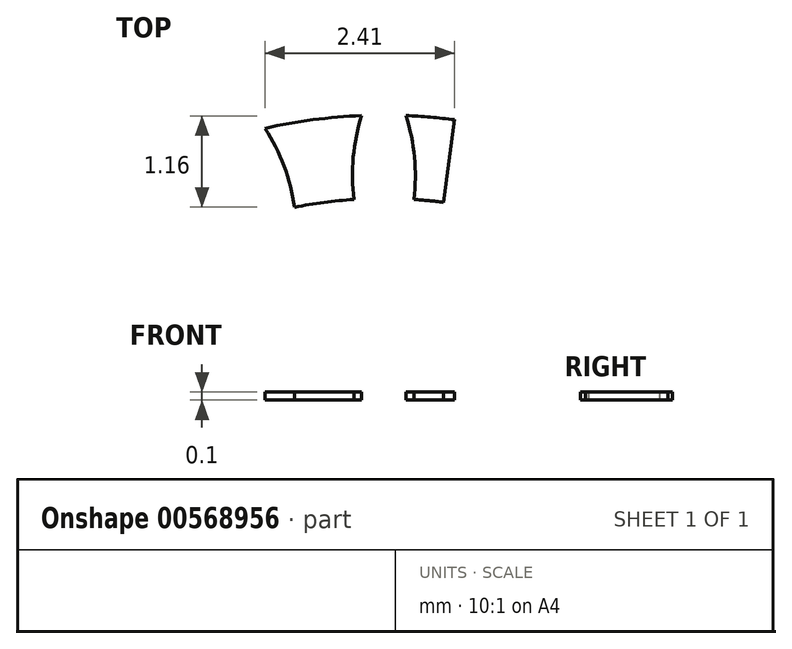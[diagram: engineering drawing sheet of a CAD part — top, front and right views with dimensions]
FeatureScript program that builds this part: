
annotation { "Feature Type Name" : "Feature", "Feature Type Description" : "" }
export const myFeature = defineFeature(function(context is Context, id is Id, definition is map)
    precondition{}
    {
        {
            var Q0;
            Q0=qCreatedBy(makeId("Top.planeOp"),FACE);
            var sketch = newSketch(context, id + "F0", { "sketchPlane" : qUnion([Q0])});
            skCircle(sketch, "E0", {"center": v(0, 0) * mm, "radius": 1.9 * mm});
            skCircle(sketch, "E1.0", {"center": v(0, 0) * mm, "radius": 2.1 * mm});
            skCircle(sketch, "E2", {"center": v(0, 0) * mm, "radius": 6.88 * mm});
            skLineSegment(sketch, "E3", {"start": v(0, 0) * mm, "end": v(0, 6.88) * mm});
            skLineSegment(sketch, "E4", {"start": v(0, 0) * mm, "end": v(0.9, 6.82) * mm});
            skPoint(sketch, "E5", {"position": v(0.38, 5.8) * mm});
            skPoint(sketch, "E6", {"position": v(0.39, 6.34) * mm});
            skPoint(sketch, "E7", {"position": v(0.28, 6.87) * mm});
            skArc(sketch, "E8", {"start": v(0.38, 5.8) * mm, "mid": v(0.57, 5.8) * mm, "end": v(0.76, 5.77) * mm});
            skArc(sketch, "E9", {"start": v(0, 6.88) * mm, "mid": v(0.14, 6.88) * mm, "end": v(0.28, 6.87) * mm});
            skArc(sketch, "E10", {"start": v(0.38, 5.8) * mm, "mid": v(0.39, 6.35) * mm, "end": v(0.28, 6.87) * mm});
            skArc(sketch, "E11.MirrorCS", {"start": v(0, 6.88) * mm, "mid": v(-0.14, 6.88) * mm, "end": v(-0.28, 6.87) * mm});
            skPoint(sketch, "E12.MirrorP", {"position": v(-0.28, 6.87) * mm});
            skPoint(sketch, "E13.MirrorP", {"position": v(-0.38, 5.8) * mm});
            skArc(sketch, "E14.MirrorCS", {"start": v(-0.38, 5.8) * mm, "mid": v(-0.39, 6.35) * mm, "end": v(-0.28, 6.87) * mm});
            skPoint(sketch, "E15.MirrorP", {"position": v(-0.39, 6.34) * mm});
            skArc(sketch, "E16.MirrorCS", {"start": v(-0.38, 5.8) * mm, "mid": v(-0.57, 5.8) * mm, "end": v(-0.76, 5.77) * mm});
            skPoint(sketch, "E17.1.0", {"position": v(-1.87, 5.51) * mm});
            skArc(sketch, "E17.1.1", {"start": v(-1.14, 5.7) * mm, "mid": v(-0.95, 5.74) * mm, "end": v(-0.76, 5.77) * mm});
            skPoint(sketch, "E17.1.2", {"position": v(-1.26, 6.22) * mm});
            skPoint(sketch, "E17.1.3", {"position": v(-2.02, 6.02) * mm});
            skArc(sketch, "E17.1.4", {"start": v(-1.14, 5.7) * mm, "mid": v(-1.27, 6.23) * mm, "end": v(-1.5, 6.71) * mm});
            skPoint(sketch, "E17.1.5", {"position": v(-2.05, 6.57) * mm});
            skPoint(sketch, "E17.1.6", {"position": v(-1.14, 5.7) * mm});
            skArc(sketch, "E17.1.7", {"start": v(-1.87, 5.51) * mm, "mid": v(-2.02, 6.03) * mm, "end": v(-2.05, 6.57) * mm});
            skArc(sketch, "E17.1.8", {"start": v(-1.87, 5.51) * mm, "mid": v(-2.05, 5.45) * mm, "end": v(-2.23, 5.38) * mm});
            skPoint(sketch, "E17.1.9", {"position": v(-1.5, 6.71) * mm});
            skArc(sketch, "E17.1.10", {"start": v(-1.78, 6.64) * mm, "mid": v(-1.64, 6.68) * mm, "end": v(-1.5, 6.71) * mm});
            skArc(sketch, "E17.1.11", {"start": v(-1.78, 6.64) * mm, "mid": v(-1.92, 6.6) * mm, "end": v(-2.05, 6.57) * mm});
            skPoint(sketch, "E17.2.0", {"position": v(-3.23, 4.84) * mm});
            skArc(sketch, "E17.2.1", {"start": v(-2.57, 5.22) * mm, "mid": v(-2.4, 5.3) * mm, "end": v(-2.23, 5.38) * mm});
            skPoint(sketch, "E17.2.2", {"position": v(-2.83, 5.68) * mm});
            skPoint(sketch, "E17.2.3", {"position": v(-3.5, 5.3) * mm});
            skArc(sketch, "E17.2.4", {"start": v(-2.57, 5.22) * mm, "mid": v(-2.84, 5.7) * mm, "end": v(-3.2, 6.1) * mm});
            skPoint(sketch, "E17.2.5", {"position": v(-3.68, 5.81) * mm});
            skPoint(sketch, "E17.2.6", {"position": v(-2.57, 5.22) * mm});
            skArc(sketch, "E17.2.7", {"start": v(-3.23, 4.84) * mm, "mid": v(-3.5, 5.3) * mm, "end": v(-3.68, 5.81) * mm});
            skArc(sketch, "E17.2.8", {"start": v(-3.23, 4.84) * mm, "mid": v(-3.4, 4.73) * mm, "end": v(-3.54, 4.62) * mm});
            skPoint(sketch, "E17.2.9", {"position": v(-3.2, 6.1) * mm});
            skArc(sketch, "E17.2.10", {"start": v(-3.44, 5.96) * mm, "mid": v(-3.32, 6.03) * mm, "end": v(-3.2, 6.1) * mm});
            skArc(sketch, "E17.2.11", {"start": v(-3.44, 5.96) * mm, "mid": v(-3.56, 5.89) * mm, "end": v(-3.68, 5.81) * mm});
            skPoint(sketch, "E17.3.0", {"position": v(-4.38, 3.84) * mm});
            skArc(sketch, "E17.3.1", {"start": v(-3.84, 4.38) * mm, "mid": v(-3.7, 4.5) * mm, "end": v(-3.54, 4.62) * mm});
            skPoint(sketch, "E17.3.2", {"position": v(-4.2, 4.76) * mm});
            skPoint(sketch, "E17.3.3", {"position": v(-4.76, 4.2) * mm});
            skArc(sketch, "E17.3.4", {"start": v(-3.84, 4.38) * mm, "mid": v(-4.21, 4.76) * mm, "end": v(-4.66, 5.06) * mm});
            skPoint(sketch, "E17.3.5", {"position": v(-5.06, 4.66) * mm});
            skPoint(sketch, "E17.3.6", {"position": v(-3.84, 4.38) * mm});
            skArc(sketch, "E17.3.7", {"start": v(-4.38, 3.84) * mm, "mid": v(-4.76, 4.21) * mm, "end": v(-5.06, 4.66) * mm});
            skArc(sketch, "E17.3.8", {"start": v(-4.38, 3.84) * mm, "mid": v(-4.5, 3.7) * mm, "end": v(-4.62, 3.54) * mm});
            skPoint(sketch, "E17.3.9", {"position": v(-4.66, 5.06) * mm});
            skArc(sketch, "E17.3.10", {"start": v(-4.86, 4.86) * mm, "mid": v(-4.76, 4.96) * mm, "end": v(-4.66, 5.06) * mm});
            skArc(sketch, "E17.3.11", {"start": v(-4.86, 4.86) * mm, "mid": v(-4.96, 4.76) * mm, "end": v(-5.06, 4.66) * mm});
            skPoint(sketch, "E17.4.0", {"position": v(-5.22, 2.57) * mm});
            skArc(sketch, "E17.4.1", {"start": v(-4.84, 3.23) * mm, "mid": v(-4.73, 3.4) * mm, "end": v(-4.62, 3.54) * mm});
            skPoint(sketch, "E17.4.2", {"position": v(-5.3, 3.5) * mm});
            skPoint(sketch, "E17.4.3", {"position": v(-5.68, 2.83) * mm});
            skArc(sketch, "E17.4.4", {"start": v(-4.84, 3.23) * mm, "mid": v(-5.3, 3.5) * mm, "end": v(-5.81, 3.68) * mm});
            skPoint(sketch, "E17.4.5", {"position": v(-6.1, 3.2) * mm});
            skPoint(sketch, "E17.4.6", {"position": v(-4.84, 3.23) * mm});
            skArc(sketch, "E17.4.7", {"start": v(-5.22, 2.57) * mm, "mid": v(-5.7, 2.84) * mm, "end": v(-6.1, 3.2) * mm});
            skArc(sketch, "E17.4.8", {"start": v(-5.22, 2.57) * mm, "mid": v(-5.3, 2.4) * mm, "end": v(-5.38, 2.23) * mm});
            skPoint(sketch, "E17.4.9", {"position": v(-5.81, 3.68) * mm});
            skArc(sketch, "E17.4.10", {"start": v(-5.96, 3.44) * mm, "mid": v(-5.89, 3.56) * mm, "end": v(-5.81, 3.68) * mm});
            skArc(sketch, "E17.4.11", {"start": v(-5.96, 3.44) * mm, "mid": v(-6.03, 3.32) * mm, "end": v(-6.1, 3.2) * mm});
            skPoint(sketch, "E17.5.0", {"position": v(-5.7, 1.14) * mm});
            skArc(sketch, "E17.5.1", {"start": v(-5.51, 1.87) * mm, "mid": v(-5.45, 2.05) * mm, "end": v(-5.38, 2.23) * mm});
            skPoint(sketch, "E17.5.2", {"position": v(-6.02, 2.02) * mm});
            skPoint(sketch, "E17.5.3", {"position": v(-6.22, 1.26) * mm});
            skArc(sketch, "E17.5.4", {"start": v(-5.51, 1.87) * mm, "mid": v(-6.03, 2.02) * mm, "end": v(-6.57, 2.05) * mm});
            skPoint(sketch, "E17.5.5", {"position": v(-6.71, 1.5) * mm});
            skPoint(sketch, "E17.5.6", {"position": v(-5.51, 1.87) * mm});
            skArc(sketch, "E17.5.7", {"start": v(-5.7, 1.14) * mm, "mid": v(-6.23, 1.27) * mm, "end": v(-6.71, 1.5) * mm});
            skArc(sketch, "E17.5.8", {"start": v(-5.7, 1.14) * mm, "mid": v(-5.74, 0.95) * mm, "end": v(-5.77, 0.76) * mm});
            skPoint(sketch, "E17.5.9", {"position": v(-6.57, 2.05) * mm});
            skArc(sketch, "E17.5.10", {"start": v(-6.64, 1.78) * mm, "mid": v(-6.6, 1.92) * mm, "end": v(-6.57, 2.05) * mm});
            skArc(sketch, "E17.5.11", {"start": v(-6.64, 1.78) * mm, "mid": v(-6.68, 1.64) * mm, "end": v(-6.71, 1.5) * mm});
            skPoint(sketch, "E17.6.0", {"position": v(-5.8, -0.38) * mm});
            skArc(sketch, "E17.6.1", {"start": v(-5.8, 0.38) * mm, "mid": v(-5.8, 0.57) * mm, "end": v(-5.77, 0.76) * mm});
            skPoint(sketch, "E17.6.2", {"position": v(-6.34, 0.39) * mm});
            skPoint(sketch, "E17.6.3", {"position": v(-6.34, -0.39) * mm});
            skArc(sketch, "E17.6.4", {"start": v(-5.8, 0.38) * mm, "mid": v(-6.35, 0.39) * mm, "end": v(-6.87, 0.28) * mm});
            skPoint(sketch, "E17.6.5", {"position": v(-6.87, -0.28) * mm});
            skPoint(sketch, "E17.6.6", {"position": v(-5.8, 0.38) * mm});
            skArc(sketch, "E17.6.7", {"start": v(-5.8, -0.38) * mm, "mid": v(-6.35, -0.39) * mm, "end": v(-6.87, -0.28) * mm});
            skArc(sketch, "E17.6.8", {"start": v(-5.8, -0.38) * mm, "mid": v(-5.8, -0.57) * mm, "end": v(-5.77, -0.76) * mm});
            skPoint(sketch, "E17.6.9", {"position": v(-6.87, 0.28) * mm});
            skArc(sketch, "E17.6.10", {"start": v(-6.88, 0) * mm, "mid": v(-6.88, 0.14) * mm, "end": v(-6.87, 0.28) * mm});
            skArc(sketch, "E17.6.11", {"start": v(-6.88, 0) * mm, "mid": v(-6.88, -0.14) * mm, "end": v(-6.87, -0.28) * mm});
            skPoint(sketch, "E17.7.0", {"position": v(-5.51, -1.87) * mm});
            skArc(sketch, "E17.7.1", {"start": v(-5.7, -1.14) * mm, "mid": v(-5.74, -0.95) * mm, "end": v(-5.77, -0.76) * mm});
            skPoint(sketch, "E17.7.2", {"position": v(-6.22, -1.26) * mm});
            skPoint(sketch, "E17.7.3", {"position": v(-6.02, -2.02) * mm});
            skArc(sketch, "E17.7.4", {"start": v(-5.7, -1.14) * mm, "mid": v(-6.23, -1.27) * mm, "end": v(-6.71, -1.5) * mm});
            skPoint(sketch, "E17.7.5", {"position": v(-6.57, -2.05) * mm});
            skPoint(sketch, "E17.7.6", {"position": v(-5.7, -1.14) * mm});
            skArc(sketch, "E17.7.7", {"start": v(-5.51, -1.87) * mm, "mid": v(-6.03, -2.02) * mm, "end": v(-6.57, -2.05) * mm});
            skArc(sketch, "E17.7.8", {"start": v(-5.51, -1.87) * mm, "mid": v(-5.45, -2.05) * mm, "end": v(-5.38, -2.23) * mm});
            skPoint(sketch, "E17.7.9", {"position": v(-6.71, -1.5) * mm});
            skArc(sketch, "E17.7.10", {"start": v(-6.64, -1.78) * mm, "mid": v(-6.68, -1.64) * mm, "end": v(-6.71, -1.5) * mm});
            skArc(sketch, "E17.7.11", {"start": v(-6.64, -1.78) * mm, "mid": v(-6.6, -1.92) * mm, "end": v(-6.57, -2.05) * mm});
            skPoint(sketch, "E17.8.0", {"position": v(-4.84, -3.23) * mm});
            skArc(sketch, "E17.8.1", {"start": v(-5.22, -2.57) * mm, "mid": v(-5.3, -2.4) * mm, "end": v(-5.38, -2.23) * mm});
            skPoint(sketch, "E17.8.2", {"position": v(-5.68, -2.83) * mm});
            skPoint(sketch, "E17.8.3", {"position": v(-5.3, -3.5) * mm});
            skArc(sketch, "E17.8.4", {"start": v(-5.22, -2.57) * mm, "mid": v(-5.7, -2.84) * mm, "end": v(-6.1, -3.2) * mm});
            skPoint(sketch, "E17.8.5", {"position": v(-5.81, -3.68) * mm});
            skPoint(sketch, "E17.8.6", {"position": v(-5.22, -2.57) * mm});
            skArc(sketch, "E17.8.7", {"start": v(-4.84, -3.23) * mm, "mid": v(-5.3, -3.5) * mm, "end": v(-5.81, -3.68) * mm});
            skArc(sketch, "E17.8.8", {"start": v(-4.84, -3.23) * mm, "mid": v(-4.73, -3.4) * mm, "end": v(-4.62, -3.54) * mm});
            skPoint(sketch, "E17.8.9", {"position": v(-6.1, -3.2) * mm});
            skArc(sketch, "E17.8.10", {"start": v(-5.96, -3.44) * mm, "mid": v(-6.03, -3.32) * mm, "end": v(-6.1, -3.2) * mm});
            skArc(sketch, "E17.8.11", {"start": v(-5.96, -3.44) * mm, "mid": v(-5.89, -3.56) * mm, "end": v(-5.81, -3.68) * mm});
            skPoint(sketch, "E17.9.0", {"position": v(-3.84, -4.38) * mm});
            skArc(sketch, "E17.9.1", {"start": v(-4.38, -3.84) * mm, "mid": v(-4.5, -3.7) * mm, "end": v(-4.62, -3.54) * mm});
            skPoint(sketch, "E17.9.2", {"position": v(-4.76, -4.2) * mm});
            skPoint(sketch, "E17.9.3", {"position": v(-4.2, -4.76) * mm});
            skArc(sketch, "E17.9.4", {"start": v(-4.38, -3.84) * mm, "mid": v(-4.76, -4.21) * mm, "end": v(-5.06, -4.66) * mm});
            skPoint(sketch, "E17.9.5", {"position": v(-4.66, -5.06) * mm});
            skPoint(sketch, "E17.9.6", {"position": v(-4.38, -3.84) * mm});
            skArc(sketch, "E17.9.7", {"start": v(-3.84, -4.38) * mm, "mid": v(-4.21, -4.76) * mm, "end": v(-4.66, -5.06) * mm});
            skArc(sketch, "E17.9.8", {"start": v(-3.84, -4.38) * mm, "mid": v(-3.7, -4.5) * mm, "end": v(-3.54, -4.62) * mm});
            skPoint(sketch, "E17.9.9", {"position": v(-5.06, -4.66) * mm});
            skArc(sketch, "E17.9.10", {"start": v(-4.86, -4.86) * mm, "mid": v(-4.96, -4.76) * mm, "end": v(-5.06, -4.66) * mm});
            skArc(sketch, "E17.9.11", {"start": v(-4.86, -4.86) * mm, "mid": v(-4.76, -4.96) * mm, "end": v(-4.66, -5.06) * mm});
            skPoint(sketch, "E17.10.0", {"position": v(-2.57, -5.22) * mm});
            skArc(sketch, "E17.10.1", {"start": v(-3.23, -4.84) * mm, "mid": v(-3.4, -4.73) * mm, "end": v(-3.54, -4.62) * mm});
            skPoint(sketch, "E17.10.2", {"position": v(-3.5, -5.3) * mm});
            skPoint(sketch, "E17.10.3", {"position": v(-2.83, -5.68) * mm});
            skArc(sketch, "E17.10.4", {"start": v(-3.23, -4.84) * mm, "mid": v(-3.5, -5.3) * mm, "end": v(-3.68, -5.81) * mm});
            skPoint(sketch, "E17.10.5", {"position": v(-3.2, -6.1) * mm});
            skPoint(sketch, "E17.10.6", {"position": v(-3.23, -4.84) * mm});
            skArc(sketch, "E17.10.7", {"start": v(-2.57, -5.22) * mm, "mid": v(-2.84, -5.7) * mm, "end": v(-3.2, -6.1) * mm});
            skArc(sketch, "E17.10.8", {"start": v(-2.57, -5.22) * mm, "mid": v(-2.4, -5.3) * mm, "end": v(-2.23, -5.38) * mm});
            skPoint(sketch, "E17.10.9", {"position": v(-3.68, -5.81) * mm});
            skArc(sketch, "E17.10.10", {"start": v(-3.44, -5.96) * mm, "mid": v(-3.56, -5.89) * mm, "end": v(-3.68, -5.81) * mm});
            skArc(sketch, "E17.10.11", {"start": v(-3.44, -5.96) * mm, "mid": v(-3.32, -6.03) * mm, "end": v(-3.2, -6.1) * mm});
            skPoint(sketch, "E17.11.0", {"position": v(-1.14, -5.7) * mm});
            skArc(sketch, "E17.11.1", {"start": v(-1.87, -5.51) * mm, "mid": v(-2.05, -5.45) * mm, "end": v(-2.23, -5.38) * mm});
            skPoint(sketch, "E17.11.2", {"position": v(-2.02, -6.02) * mm});
            skPoint(sketch, "E17.11.3", {"position": v(-1.26, -6.22) * mm});
            skArc(sketch, "E17.11.4", {"start": v(-1.87, -5.51) * mm, "mid": v(-2.02, -6.03) * mm, "end": v(-2.05, -6.57) * mm});
            skPoint(sketch, "E17.11.5", {"position": v(-1.5, -6.71) * mm});
            skPoint(sketch, "E17.11.6", {"position": v(-1.87, -5.51) * mm});
            skArc(sketch, "E17.11.7", {"start": v(-1.14, -5.7) * mm, "mid": v(-1.27, -6.23) * mm, "end": v(-1.5, -6.71) * mm});
            skArc(sketch, "E17.11.8", {"start": v(-1.14, -5.7) * mm, "mid": v(-0.95, -5.74) * mm, "end": v(-0.76, -5.77) * mm});
            skPoint(sketch, "E17.11.9", {"position": v(-2.05, -6.57) * mm});
            skArc(sketch, "E17.11.10", {"start": v(-1.78, -6.64) * mm, "mid": v(-1.92, -6.6) * mm, "end": v(-2.05, -6.57) * mm});
            skArc(sketch, "E17.11.11", {"start": v(-1.78, -6.64) * mm, "mid": v(-1.64, -6.68) * mm, "end": v(-1.5, -6.71) * mm});
            skPoint(sketch, "E17.12.0", {"position": v(0.38, -5.8) * mm});
            skArc(sketch, "E17.12.1", {"start": v(-0.38, -5.8) * mm, "mid": v(-0.57, -5.8) * mm, "end": v(-0.76, -5.77) * mm});
            skPoint(sketch, "E17.12.2", {"position": v(-0.39, -6.34) * mm});
            skPoint(sketch, "E17.12.3", {"position": v(0.39, -6.34) * mm});
            skArc(sketch, "E17.12.4", {"start": v(-0.38, -5.8) * mm, "mid": v(-0.39, -6.35) * mm, "end": v(-0.28, -6.87) * mm});
            skPoint(sketch, "E17.12.5", {"position": v(0.28, -6.87) * mm});
            skPoint(sketch, "E17.12.6", {"position": v(-0.38, -5.8) * mm});
            skArc(sketch, "E17.12.7", {"start": v(0.38, -5.8) * mm, "mid": v(0.39, -6.35) * mm, "end": v(0.28, -6.87) * mm});
            skArc(sketch, "E17.12.8", {"start": v(0.38, -5.8) * mm, "mid": v(0.57, -5.8) * mm, "end": v(0.76, -5.77) * mm});
            skPoint(sketch, "E17.12.9", {"position": v(-0.28, -6.87) * mm});
            skArc(sketch, "E17.12.10", {"start": v(0, -6.88) * mm, "mid": v(-0.14, -6.88) * mm, "end": v(-0.28, -6.87) * mm});
            skArc(sketch, "E17.12.11", {"start": v(0, -6.88) * mm, "mid": v(0.14, -6.88) * mm, "end": v(0.28, -6.87) * mm});
            skPoint(sketch, "E17.13.0", {"position": v(1.87, -5.51) * mm});
            skArc(sketch, "E17.13.1", {"start": v(1.14, -5.7) * mm, "mid": v(0.95, -5.74) * mm, "end": v(0.76, -5.77) * mm});
            skPoint(sketch, "E17.13.2", {"position": v(1.26, -6.22) * mm});
            skPoint(sketch, "E17.13.3", {"position": v(2.02, -6.02) * mm});
            skArc(sketch, "E17.13.4", {"start": v(1.14, -5.7) * mm, "mid": v(1.27, -6.23) * mm, "end": v(1.5, -6.71) * mm});
            skPoint(sketch, "E17.13.5", {"position": v(2.05, -6.57) * mm});
            skPoint(sketch, "E17.13.6", {"position": v(1.14, -5.7) * mm});
            skArc(sketch, "E17.13.7", {"start": v(1.87, -5.51) * mm, "mid": v(2.02, -6.03) * mm, "end": v(2.05, -6.57) * mm});
            skArc(sketch, "E17.13.8", {"start": v(1.87, -5.51) * mm, "mid": v(2.05, -5.45) * mm, "end": v(2.23, -5.38) * mm});
            skPoint(sketch, "E17.13.9", {"position": v(1.5, -6.71) * mm});
            skArc(sketch, "E17.13.10", {"start": v(1.78, -6.64) * mm, "mid": v(1.64, -6.68) * mm, "end": v(1.5, -6.71) * mm});
            skArc(sketch, "E17.13.11", {"start": v(1.78, -6.64) * mm, "mid": v(1.92, -6.6) * mm, "end": v(2.05, -6.57) * mm});
            skPoint(sketch, "E17.14.0", {"position": v(3.23, -4.84) * mm});
            skArc(sketch, "E17.14.1", {"start": v(2.57, -5.22) * mm, "mid": v(2.4, -5.3) * mm, "end": v(2.23, -5.38) * mm});
            skPoint(sketch, "E17.14.2", {"position": v(2.83, -5.68) * mm});
            skPoint(sketch, "E17.14.3", {"position": v(3.5, -5.3) * mm});
            skArc(sketch, "E17.14.4", {"start": v(2.57, -5.22) * mm, "mid": v(2.84, -5.7) * mm, "end": v(3.2, -6.1) * mm});
            skPoint(sketch, "E17.14.5", {"position": v(3.68, -5.81) * mm});
            skPoint(sketch, "E17.14.6", {"position": v(2.57, -5.22) * mm});
            skArc(sketch, "E17.14.7", {"start": v(3.23, -4.84) * mm, "mid": v(3.5, -5.3) * mm, "end": v(3.68, -5.81) * mm});
            skArc(sketch, "E17.14.8", {"start": v(3.23, -4.84) * mm, "mid": v(3.4, -4.73) * mm, "end": v(3.54, -4.62) * mm});
            skPoint(sketch, "E17.14.9", {"position": v(3.2, -6.1) * mm});
            skArc(sketch, "E17.14.10", {"start": v(3.44, -5.96) * mm, "mid": v(3.32, -6.03) * mm, "end": v(3.2, -6.1) * mm});
            skArc(sketch, "E17.14.11", {"start": v(3.44, -5.96) * mm, "mid": v(3.56, -5.89) * mm, "end": v(3.68, -5.81) * mm});
            skPoint(sketch, "E17.15.0", {"position": v(4.38, -3.84) * mm});
            skArc(sketch, "E17.15.1", {"start": v(3.84, -4.38) * mm, "mid": v(3.7, -4.5) * mm, "end": v(3.54, -4.62) * mm});
            skPoint(sketch, "E17.15.2", {"position": v(4.2, -4.76) * mm});
            skPoint(sketch, "E17.15.3", {"position": v(4.76, -4.2) * mm});
            skArc(sketch, "E17.15.4", {"start": v(3.84, -4.38) * mm, "mid": v(4.21, -4.76) * mm, "end": v(4.66, -5.06) * mm});
            skPoint(sketch, "E17.15.5", {"position": v(5.06, -4.66) * mm});
            skPoint(sketch, "E17.15.6", {"position": v(3.84, -4.38) * mm});
            skArc(sketch, "E17.15.7", {"start": v(4.38, -3.84) * mm, "mid": v(4.76, -4.21) * mm, "end": v(5.06, -4.66) * mm});
            skArc(sketch, "E17.15.8", {"start": v(4.38, -3.84) * mm, "mid": v(4.5, -3.7) * mm, "end": v(4.62, -3.54) * mm});
            skPoint(sketch, "E17.15.9", {"position": v(4.66, -5.06) * mm});
            skArc(sketch, "E17.15.10", {"start": v(4.86, -4.86) * mm, "mid": v(4.76, -4.96) * mm, "end": v(4.66, -5.06) * mm});
            skArc(sketch, "E17.15.11", {"start": v(4.86, -4.86) * mm, "mid": v(4.96, -4.76) * mm, "end": v(5.06, -4.66) * mm});
            skPoint(sketch, "E17.16.0", {"position": v(5.22, -2.57) * mm});
            skArc(sketch, "E17.16.1", {"start": v(4.84, -3.23) * mm, "mid": v(4.73, -3.4) * mm, "end": v(4.62, -3.54) * mm});
            skPoint(sketch, "E17.16.2", {"position": v(5.3, -3.5) * mm});
            skPoint(sketch, "E17.16.3", {"position": v(5.68, -2.83) * mm});
            skArc(sketch, "E17.16.4", {"start": v(4.84, -3.23) * mm, "mid": v(5.3, -3.5) * mm, "end": v(5.81, -3.68) * mm});
            skPoint(sketch, "E17.16.5", {"position": v(6.1, -3.2) * mm});
            skPoint(sketch, "E17.16.6", {"position": v(4.84, -3.23) * mm});
            skArc(sketch, "E17.16.7", {"start": v(5.22, -2.57) * mm, "mid": v(5.7, -2.84) * mm, "end": v(6.1, -3.2) * mm});
            skArc(sketch, "E17.16.8", {"start": v(5.22, -2.57) * mm, "mid": v(5.3, -2.4) * mm, "end": v(5.38, -2.23) * mm});
            skPoint(sketch, "E17.16.9", {"position": v(5.81, -3.68) * mm});
            skArc(sketch, "E17.16.10", {"start": v(5.96, -3.44) * mm, "mid": v(5.89, -3.56) * mm, "end": v(5.81, -3.68) * mm});
            skArc(sketch, "E17.16.11", {"start": v(5.96, -3.44) * mm, "mid": v(6.03, -3.32) * mm, "end": v(6.1, -3.2) * mm});
            skPoint(sketch, "E17.17.0", {"position": v(5.7, -1.14) * mm});
            skArc(sketch, "E17.17.1", {"start": v(5.51, -1.87) * mm, "mid": v(5.45, -2.05) * mm, "end": v(5.38, -2.23) * mm});
            skPoint(sketch, "E17.17.2", {"position": v(6.02, -2.02) * mm});
            skPoint(sketch, "E17.17.3", {"position": v(6.22, -1.26) * mm});
            skArc(sketch, "E17.17.4", {"start": v(5.51, -1.87) * mm, "mid": v(6.03, -2.02) * mm, "end": v(6.57, -2.05) * mm});
            skPoint(sketch, "E17.17.5", {"position": v(6.71, -1.5) * mm});
            skPoint(sketch, "E17.17.6", {"position": v(5.51, -1.87) * mm});
            skArc(sketch, "E17.17.7", {"start": v(5.7, -1.14) * mm, "mid": v(6.23, -1.27) * mm, "end": v(6.71, -1.5) * mm});
            skArc(sketch, "E17.17.8", {"start": v(5.7, -1.14) * mm, "mid": v(5.74, -0.95) * mm, "end": v(5.77, -0.76) * mm});
            skPoint(sketch, "E17.17.9", {"position": v(6.57, -2.05) * mm});
            skArc(sketch, "E17.17.10", {"start": v(6.64, -1.78) * mm, "mid": v(6.6, -1.92) * mm, "end": v(6.57, -2.05) * mm});
            skArc(sketch, "E17.17.11", {"start": v(6.64, -1.78) * mm, "mid": v(6.68, -1.64) * mm, "end": v(6.71, -1.5) * mm});
            skPoint(sketch, "E17.18.0", {"position": v(5.8, 0.38) * mm});
            skArc(sketch, "E17.18.1", {"start": v(5.8, -0.38) * mm, "mid": v(5.8, -0.57) * mm, "end": v(5.77, -0.76) * mm});
            skPoint(sketch, "E17.18.2", {"position": v(6.34, -0.39) * mm});
            skPoint(sketch, "E17.18.3", {"position": v(6.34, 0.39) * mm});
            skArc(sketch, "E17.18.4", {"start": v(5.8, -0.38) * mm, "mid": v(6.35, -0.39) * mm, "end": v(6.87, -0.28) * mm});
            skPoint(sketch, "E17.18.5", {"position": v(6.87, 0.28) * mm});
            skPoint(sketch, "E17.18.6", {"position": v(5.8, -0.38) * mm});
            skArc(sketch, "E17.18.7", {"start": v(5.8, 0.38) * mm, "mid": v(6.35, 0.39) * mm, "end": v(6.87, 0.28) * mm});
            skArc(sketch, "E17.18.8", {"start": v(5.8, 0.38) * mm, "mid": v(5.8, 0.57) * mm, "end": v(5.77, 0.76) * mm});
            skPoint(sketch, "E17.18.9", {"position": v(6.87, -0.28) * mm});
            skArc(sketch, "E17.18.10", {"start": v(6.88, 0) * mm, "mid": v(6.88, -0.14) * mm, "end": v(6.87, -0.28) * mm});
            skArc(sketch, "E17.18.11", {"start": v(6.88, 0) * mm, "mid": v(6.88, 0.14) * mm, "end": v(6.87, 0.28) * mm});
            skPoint(sketch, "E17.19.0", {"position": v(5.51, 1.87) * mm});
            skArc(sketch, "E17.19.1", {"start": v(5.7, 1.14) * mm, "mid": v(5.74, 0.95) * mm, "end": v(5.77, 0.76) * mm});
            skPoint(sketch, "E17.19.2", {"position": v(6.22, 1.26) * mm});
            skPoint(sketch, "E17.19.3", {"position": v(6.02, 2.02) * mm});
            skArc(sketch, "E17.19.4", {"start": v(5.7, 1.14) * mm, "mid": v(6.23, 1.27) * mm, "end": v(6.71, 1.5) * mm});
            skPoint(sketch, "E17.19.5", {"position": v(6.57, 2.05) * mm});
            skPoint(sketch, "E17.19.6", {"position": v(5.7, 1.14) * mm});
            skArc(sketch, "E17.19.7", {"start": v(5.51, 1.87) * mm, "mid": v(6.03, 2.02) * mm, "end": v(6.57, 2.05) * mm});
            skArc(sketch, "E17.19.8", {"start": v(5.51, 1.87) * mm, "mid": v(5.45, 2.05) * mm, "end": v(5.38, 2.23) * mm});
            skPoint(sketch, "E17.19.9", {"position": v(6.71, 1.5) * mm});
            skArc(sketch, "E17.19.10", {"start": v(6.64, 1.78) * mm, "mid": v(6.68, 1.64) * mm, "end": v(6.71, 1.5) * mm});
            skArc(sketch, "E17.19.11", {"start": v(6.64, 1.78) * mm, "mid": v(6.6, 1.92) * mm, "end": v(6.57, 2.05) * mm});
            skPoint(sketch, "E17.20.0", {"position": v(4.84, 3.23) * mm});
            skArc(sketch, "E17.20.1", {"start": v(5.22, 2.57) * mm, "mid": v(5.3, 2.4) * mm, "end": v(5.38, 2.23) * mm});
            skPoint(sketch, "E17.20.2", {"position": v(5.68, 2.83) * mm});
            skPoint(sketch, "E17.20.3", {"position": v(5.3, 3.5) * mm});
            skArc(sketch, "E17.20.4", {"start": v(5.22, 2.57) * mm, "mid": v(5.7, 2.84) * mm, "end": v(6.1, 3.2) * mm});
            skPoint(sketch, "E17.20.5", {"position": v(5.81, 3.68) * mm});
            skPoint(sketch, "E17.20.6", {"position": v(5.22, 2.57) * mm});
            skArc(sketch, "E17.20.7", {"start": v(4.84, 3.23) * mm, "mid": v(5.3, 3.5) * mm, "end": v(5.81, 3.68) * mm});
            skArc(sketch, "E17.20.8", {"start": v(4.84, 3.23) * mm, "mid": v(4.73, 3.4) * mm, "end": v(4.62, 3.54) * mm});
            skPoint(sketch, "E17.20.9", {"position": v(6.1, 3.2) * mm});
            skArc(sketch, "E17.20.10", {"start": v(5.96, 3.44) * mm, "mid": v(6.03, 3.32) * mm, "end": v(6.1, 3.2) * mm});
            skArc(sketch, "E17.20.11", {"start": v(5.96, 3.44) * mm, "mid": v(5.89, 3.56) * mm, "end": v(5.81, 3.68) * mm});
            skPoint(sketch, "E17.21.0", {"position": v(3.84, 4.38) * mm});
            skArc(sketch, "E17.21.1", {"start": v(4.38, 3.84) * mm, "mid": v(4.5, 3.7) * mm, "end": v(4.62, 3.54) * mm});
            skPoint(sketch, "E17.21.2", {"position": v(4.76, 4.2) * mm});
            skPoint(sketch, "E17.21.3", {"position": v(4.2, 4.76) * mm});
            skArc(sketch, "E17.21.4", {"start": v(4.38, 3.84) * mm, "mid": v(4.76, 4.21) * mm, "end": v(5.06, 4.66) * mm});
            skPoint(sketch, "E17.21.5", {"position": v(4.66, 5.06) * mm});
            skPoint(sketch, "E17.21.6", {"position": v(4.38, 3.84) * mm});
            skArc(sketch, "E17.21.7", {"start": v(3.84, 4.38) * mm, "mid": v(4.21, 4.76) * mm, "end": v(4.66, 5.06) * mm});
            skArc(sketch, "E17.21.8", {"start": v(3.84, 4.38) * mm, "mid": v(3.7, 4.5) * mm, "end": v(3.54, 4.62) * mm});
            skPoint(sketch, "E17.21.9", {"position": v(5.06, 4.66) * mm});
            skArc(sketch, "E17.21.10", {"start": v(4.86, 4.86) * mm, "mid": v(4.96, 4.76) * mm, "end": v(5.06, 4.66) * mm});
            skArc(sketch, "E17.21.11", {"start": v(4.86, 4.86) * mm, "mid": v(4.76, 4.96) * mm, "end": v(4.66, 5.06) * mm});
            skPoint(sketch, "E17.22.0", {"position": v(2.57, 5.22) * mm});
            skArc(sketch, "E17.22.1", {"start": v(3.23, 4.84) * mm, "mid": v(3.4, 4.73) * mm, "end": v(3.54, 4.62) * mm});
            skPoint(sketch, "E17.22.2", {"position": v(3.5, 5.3) * mm});
            skPoint(sketch, "E17.22.3", {"position": v(2.83, 5.68) * mm});
            skArc(sketch, "E17.22.4", {"start": v(3.23, 4.84) * mm, "mid": v(3.5, 5.3) * mm, "end": v(3.68, 5.81) * mm});
            skPoint(sketch, "E17.22.5", {"position": v(3.2, 6.1) * mm});
            skPoint(sketch, "E17.22.6", {"position": v(3.23, 4.84) * mm});
            skArc(sketch, "E17.22.7", {"start": v(2.57, 5.22) * mm, "mid": v(2.84, 5.7) * mm, "end": v(3.2, 6.1) * mm});
            skArc(sketch, "E17.22.8", {"start": v(2.57, 5.22) * mm, "mid": v(2.4, 5.3) * mm, "end": v(2.23, 5.38) * mm});
            skPoint(sketch, "E17.22.9", {"position": v(3.68, 5.81) * mm});
            skArc(sketch, "E17.22.10", {"start": v(3.44, 5.96) * mm, "mid": v(3.56, 5.89) * mm, "end": v(3.68, 5.81) * mm});
            skArc(sketch, "E17.22.11", {"start": v(3.44, 5.96) * mm, "mid": v(3.32, 6.03) * mm, "end": v(3.2, 6.1) * mm});
            skPoint(sketch, "E17.23.0", {"position": v(1.14, 5.7) * mm});
            skArc(sketch, "E17.23.1", {"start": v(1.87, 5.51) * mm, "mid": v(2.05, 5.45) * mm, "end": v(2.23, 5.38) * mm});
            skPoint(sketch, "E17.23.2", {"position": v(2.02, 6.02) * mm});
            skPoint(sketch, "E17.23.3", {"position": v(1.26, 6.22) * mm});
            skArc(sketch, "E17.23.4", {"start": v(1.87, 5.51) * mm, "mid": v(2.02, 6.03) * mm, "end": v(2.05, 6.57) * mm});
            skPoint(sketch, "E17.23.5", {"position": v(1.5, 6.71) * mm});
            skPoint(sketch, "E17.23.6", {"position": v(1.87, 5.51) * mm});
            skArc(sketch, "E17.23.7", {"start": v(1.14, 5.7) * mm, "mid": v(1.27, 6.23) * mm, "end": v(1.5, 6.71) * mm});
            skArc(sketch, "E17.23.8", {"start": v(1.14, 5.7) * mm, "mid": v(0.95, 5.74) * mm, "end": v(0.76, 5.77) * mm});
            skPoint(sketch, "E17.23.9", {"position": v(2.05, 6.57) * mm});
            skArc(sketch, "E17.23.10", {"start": v(1.78, 6.64) * mm, "mid": v(1.92, 6.6) * mm, "end": v(2.05, 6.57) * mm});
            skArc(sketch, "E17.23.11", {"start": v(1.78, 6.64) * mm, "mid": v(1.64, 6.68) * mm, "end": v(1.5, 6.71) * mm});
            skSolve(sketch);
        }
        {
            var Q0;
            {var subQ46=sQuery(id+"F0.wireOp",EDGE,"E14.MirrorCS");Q0=makeQuery(id+"F0.imprint","IMPRINT",FACE,{"disambiguationData":[TD([[makeQuery(id+"F0.imprint","IMPRINT",EDGE,{"derivedFrom":subQ46}),-1.0]])]});}
            var Q1;
            {var subQ0=sQuery(id+"F0.wireOp",EDGE,"E8");Q1=makeQuery(id+"F0.imprint","IMPRINT",FACE,{"disambiguationData":[TD([[makeQuery(id+"F0.imprint","IMPRINT",EDGE,{"derivedFrom":subQ0}),-1.0]])]});}
            extrude(context, id + "F1", {"entities" : qUnion([Q0, Q1]), "depth" : .1 * mm, "offsetDistance" : 25.4 * mm});
        }
    });
